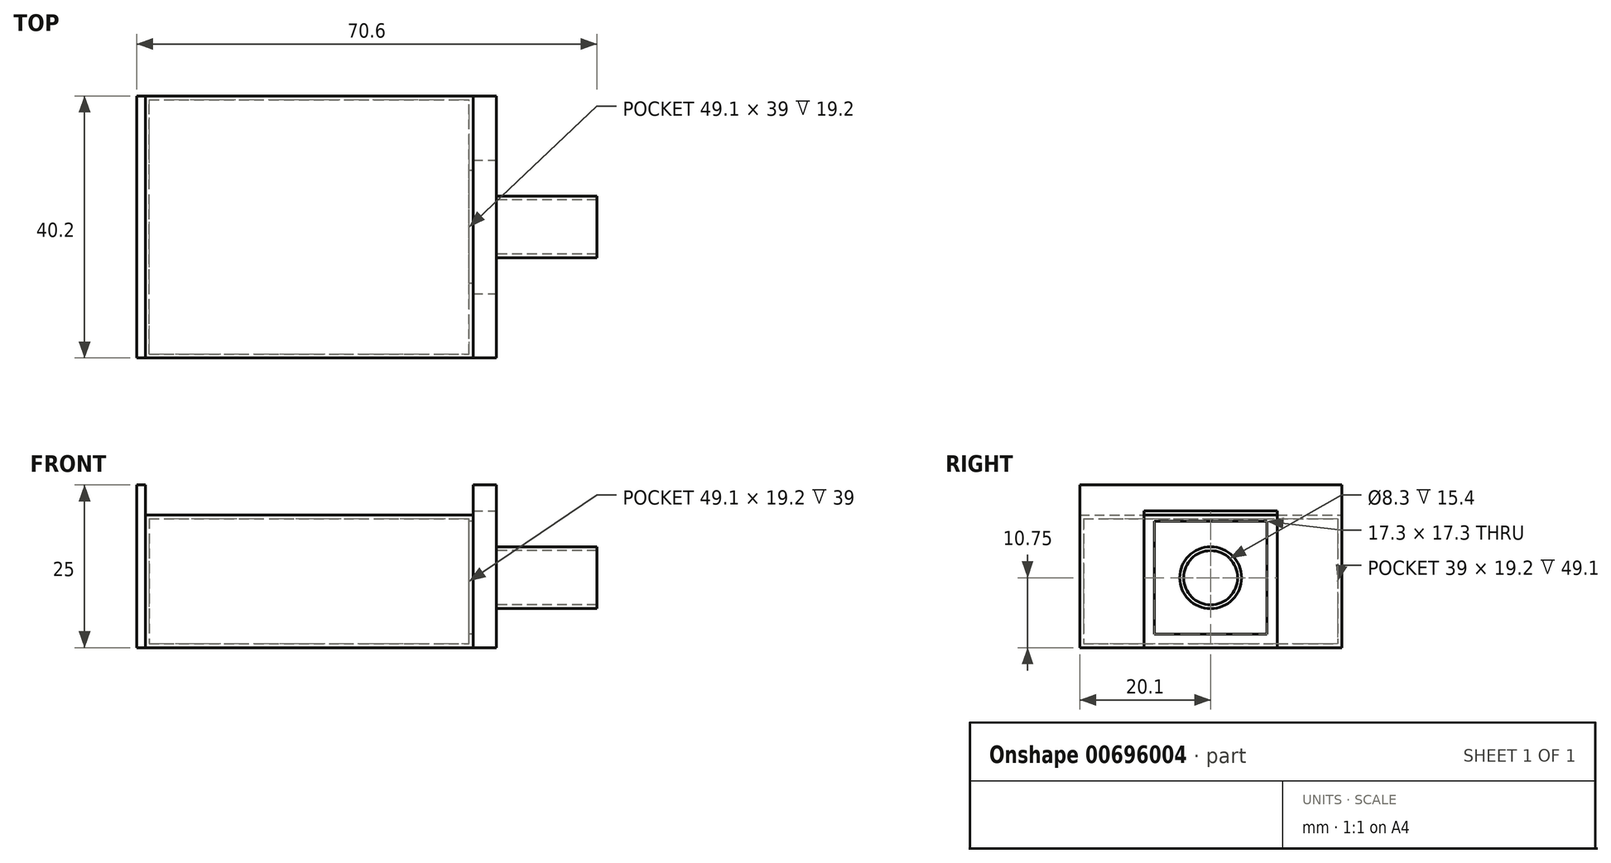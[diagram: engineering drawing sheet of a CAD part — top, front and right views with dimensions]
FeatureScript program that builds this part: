
annotation { "Feature Type Name" : "Feature", "Feature Type Description" : "" }
export const myFeature = defineFeature(function(context is Context, id is Id, definition is map)
    precondition{}
    {
        {
            var Q0;
            Q0=qCreatedBy(makeId("Front.planeOp"),FACE);
            var sketch = newSketch(context, id + "F0", { "sketchPlane" : qUnion([Q0])});
            skLineSegment(sketch, "E0", {"start": v(-22.7, 20.4) * mm, "end": v(27.6, 20.4) * mm});
            skLineSegment(sketch, "E1", {"start": v(-22.7, 20.4) * mm, "end": v(-22.7, 0) * mm});
            skLineSegment(sketch, "E2", {"start": v(-22.7, 0) * mm, "end": v(27.6, 0) * mm});
            skLineSegment(sketch, "E3", {"start": v(27.6, 0) * mm, "end": v(27.6, 20.4) * mm});
            skPoint(sketch, "E4", {"position": v(0, 0) * mm});
            skSolve(sketch);
        }
        {
            var Q0;
            Q0=makeQuery(id+"F0.imprint","IMPRINT",FACE,{"disambiguationData":[TD([[makeQuery(id+"F0.imprint","IMPRINT",EDGE,{"derivedFrom":sQuery(id+"F0.wireOp",EDGE,"E0")}),-1.0]])]});
            extrude(context, id + "F1", {"entities" : qUnion([Q0]), "depth" : 40.2 * mm, "offsetDistance" : 25 * mm, "symmetric" : true});
        }
        {
            var Q0;
            Q0=makeQuery(id+"F1.opExtrude","SWEPT_FACE",FACE,{"disambiguationData":[OSD([sQuery(id+"F0.wireOp",EDGE,"E3")])]});
            var sketch = newSketch(context, id + "F2", { "sketchPlane" : qUnion([Q0])});
            skLineSegment(sketch, "E5", {"start": v(-9.25, 1.5) * mm, "end": v(0, 1.5) * mm});
            skLineSegment(sketch, "E6", {"start": v(-9.25, 1.5) * mm, "end": v(-9.25, 20) * mm});
            skLineSegment(sketch, "E7", {"start": v(-9.25, 20) * mm, "end": v(0, 20) * mm});
            skLineSegment(sketch, "E8.MirrorCS", {"start": v(9.25, 20) * mm, "end": v(0, 20) * mm});
            skLineSegment(sketch, "E9.MirrorCS", {"start": v(9.25, 1.5) * mm, "end": v(9.25, 20) * mm});
            skLineSegment(sketch, "E10.MirrorCS", {"start": v(9.25, 1.5) * mm, "end": v(0, 1.5) * mm});
            skCircle(sketch, "E11", {"center": v(0, 10.75) * mm, "radius": 4.75 * mm});
            skPoint(sketch, "E12", {"position": v(-9.25, 10.75) * mm});
            skLineSegment(sketch, "E13", {"start": v(-9.25, 10.75) * mm, "end": v(9.25, 10.75) * mm, "construction": true});
            skSolve(sketch);
        }
        {
            var Q0;
            Q0=makeQuery(id+"F2.imprint","IMPRINT",FACE,{"disambiguationData":[TD([[makeQuery(id+"F2.imprint","IMPRINT",EDGE,{"derivedFrom":sQuery(id+"F2.wireOp",EDGE,"E5")}),1.0]])]});
            extrude(context, id + "F3", {"entities" : qUnion([Q0]), "operationType" : NewBodyOperationType.ADD, "depth" : 1.5 * mm, "offsetDistance" : 25 * mm});
        }
        {
            var Q0;
            Q0=makeQuery(id+"F3.boolean.opBoolean","SPLIT",FACE,{"disambiguationData":[TD([makeQuery(id+"F3.opExtrude","SWEPT_FACE",FACE,{"disambiguationData":[OSD([sQuery(id+"F2.wireOp",EDGE,"E11")])]})])],"derivedFrom":makeQuery(id+"F1.opExtrude","SWEPT_FACE",FACE,{"disambiguationData":[OSD([sQuery(id+"F0.wireOp",EDGE,"E3")])]})});
            extrude(context, id + "F4", {"entities" : qUnion([Q0]), "operationType" : NewBodyOperationType.ADD, "depth" : 19 * mm, "offsetDistance" : 25 * mm});
        }
        {
            var Q0;
            Q0=makeQuery(id+"F4.opExtrude","CAP_FACE",FACE,{"disambiguationData":[OSD([sQuery(id+"F0.wireOp",EDGE,"E3")])],"isStart":false});
            shell(context, id + "F5", {"entities" : qUnion([Q0]), "thickness" : .6 * mm});
        }
        {
            var Q0;
            Q0=qCreatedBy(makeId("Top.planeOp"),FACE);
            var sketch = newSketch(context, id + "F6", { "sketchPlane" : qUnion([Q0])});
            skLineSegment(sketch, "E14.bottom", {"start": v(27.6, -20.1) * mm, "end": v(31.2, -20.1) * mm});
            skLineSegment(sketch, "E14.top", {"start": v(27.6, 20.1) * mm, "end": v(31.2, 20.1) * mm});
            skLineSegment(sketch, "E14.left", {"start": v(27.6, -20.1) * mm, "end": v(27.6, 20.1) * mm});
            skLineSegment(sketch, "E14.right", {"start": v(31.2, -20.1) * mm, "end": v(31.2, 20.1) * mm});
            skLineSegment(sketch, "E15.bottom", {"start": v(-22.7, -20.1) * mm, "end": v(-24, -20.1) * mm});
            skLineSegment(sketch, "E15.top", {"start": v(-22.7, 20.1) * mm, "end": v(-24, 20.1) * mm});
            skLineSegment(sketch, "E15.left", {"start": v(-22.7, -20.1) * mm, "end": v(-22.7, 20.1) * mm});
            skLineSegment(sketch, "E15.right", {"start": v(-24, -20.1) * mm, "end": v(-24, 20.1) * mm});
            skSolve(sketch);
        }
        {
            var Q0;
            Q0=makeQuery(id+"F6.imprint","IMPRINT",FACE,{"disambiguationData":[TD([[makeQuery(id+"F6.imprint","IMPRINT",EDGE,{"derivedFrom":sQuery(id+"F6.wireOp",EDGE,"E14.bottom")}),1.0]])]});
            var Q1;
            Q1=makeQuery(id+"F6.imprint","IMPRINT",FACE,{"disambiguationData":[TD([[makeQuery(id+"F6.imprint","IMPRINT",EDGE,{"derivedFrom":sQuery(id+"F6.wireOp",EDGE,"E15.bottom")}),-1.0]])]});
            extrude(context, id + "F7", {"entities" : qUnion([Q0, Q1]), "depth" : 25 * mm, "offsetDistance" : 25 * mm});
        }
        {
            var Q0;
            Q0=makeQuery(id+"F7.opExtrude","SWEPT_FACE",FACE,{"disambiguationData":[OSD([sQuery(id+"F6.wireOp",EDGE,"E14.right")])]});
            var sketch = newSketch(context, id + "F8", { "sketchPlane" : qUnion([Q0])});
            skLineSegment(sketch, "E16.bottom", {"start": v(-9.25, 20) * mm, "end": v(9.25, 20) * mm});
            skLineSegment(sketch, "E16.top", {"start": v(-9.25, 0) * mm, "end": v(9.25, 0) * mm});
            skLineSegment(sketch, "E16.left", {"start": v(-9.25, 20) * mm, "end": v(-9.25, 0) * mm});
            skLineSegment(sketch, "E16.right", {"start": v(9.25, 20) * mm, "end": v(9.25, 0) * mm});
            skLineSegment(sketch, "E17.0", {"start": v(10.25, 21) * mm, "end": v(10.25, 0) * mm});
            skLineSegment(sketch, "E17.1", {"start": v(-10.25, 21) * mm, "end": v(10.25, 21) * mm});
            skLineSegment(sketch, "E17.2", {"start": v(-10.25, 21) * mm, "end": v(-10.25, 0) * mm});
            skLineSegment(sketch, "E18", {"start": v(0, 25) * mm, "end": v(0, 0) * mm, "construction": true});
            skLineSegment(sketch, "E19", {"start": v(0, 25) * mm, "end": v(20.1, 25) * mm, "construction": true});
            skLineSegment(sketch, "E20", {"start": v(10.05, 25) * mm, "end": v(10.05, 0) * mm, "construction": true});
            skCircle(sketch, "E21", {"center": v(10.05, 19) * mm, "radius": 3 * mm});
            skCircle(sketch, "E22", {"center": v(0, 19) * mm, "radius": 3 * mm});
            skLineSegment(sketch, "E23", {"start": v(0, 19) * mm, "end": v(20.1, 19) * mm, "construction": true});
            skCircle(sketch, "E24.MirrorC", {"center": v(-10.05, 19) * mm, "radius": 3 * mm});
            skSolve(sketch);
        }
        {
            var Q0;
            {var subQ1=makeQuery(id+"F7.opExtrude","CAP_EDGE",EDGE,{"disambiguationData":[OSD([sQuery(id+"F6.wireOp",EDGE,"E14.right")])],"isStart":true});var subQ5=sQuery(id+"F8.wireOp",EDGE,"E17.2");var subQ6=makeQuery(id+"F8.imprint","INTERSECT",VERTEX,{"derivedFrom":[subQ1,subQ5]});Q0=makeQuery(id+"F8.imprint","IMPRINT",FACE,{"disambiguationData":[TD([[makeQuery(id+"F8.imprint","IMPRINT",EDGE,{"disambiguationData":[TD([[subQ6,1.0]])],"derivedFrom":subQ5}),1.0]])]});}
            var Q1;
            {var subQ5=sQuery(id+"F8.wireOp",EDGE,"E16.left");var subQ6=sQuery(id+"F8.wireOp",EDGE,"E16.bottom");var subQ7=makeQuery(id+"F8.imprint","INTERSECT",VERTEX,{"derivedFrom":[subQ6,subQ5]});Q1=makeQuery(id+"F8.imprint","IMPRINT",FACE,{"disambiguationData":[TD([[makeQuery(id+"F8.imprint","IMPRINT",EDGE,{"disambiguationData":[TD([[subQ7,-1.0]])],"derivedFrom":subQ6}),1.0]])]});}
            var Q2;
            {var subQ0=sQuery(id+"F8.wireOp",EDGE,"E24.MirrorC");var subQ1=sQuery(id+"F8.wireOp",EDGE,"E16.bottom");var subQ2=makeQuery(id+"F8.imprint","INTERSECT",VERTEX,{"derivedFrom":[subQ1,subQ0]});Q2=makeQuery(id+"F8.imprint","IMPRINT",FACE,{"disambiguationData":[TD([[makeQuery(id+"F8.imprint","IMPRINT",EDGE,{"disambiguationData":[TD([[subQ2,-1.0]])],"derivedFrom":subQ1}),1.0]])]});}
            var Q3;
            {var subQ1=sQuery(id+"F8.wireOp",EDGE,"E16.top");Q3=makeQuery(id+"F8.imprint","IMPRINT",FACE,{"disambiguationData":[TD([[makeQuery(id+"F8.imprint","IMPRINT",EDGE,{"derivedFrom":subQ1}),1.0]])]});}
            var Q4;
            {var subQ0=sQuery(id+"F8.wireOp",EDGE,"E16.right");var subQ1=sQuery(id+"F8.wireOp",EDGE,"E16.bottom");var subQ2=makeQuery(id+"F8.imprint","INTERSECT",VERTEX,{"derivedFrom":[subQ1,subQ0]});Q4=makeQuery(id+"F8.imprint","IMPRINT",FACE,{"disambiguationData":[TD([[makeQuery(id+"F8.imprint","IMPRINT",EDGE,{"disambiguationData":[TD([[subQ2,1.0]])],"derivedFrom":subQ1}),-1.0]])]});}
            var Q5;
            {var subQ0=sQuery(id+"F8.wireOp",EDGE,"E22");var subQ1=sQuery(id+"F8.wireOp",EDGE,"E16.bottom");var subQ2=makeQuery(id+"F8.imprint","INTERSECT",VERTEX,{"disambiguationData":[OD(0.0)],"derivedFrom":[subQ1,subQ0]});Q5=makeQuery(id+"F8.imprint","IMPRINT",FACE,{"disambiguationData":[TD([[makeQuery(id+"F8.imprint","IMPRINT",EDGE,{"disambiguationData":[TD([[subQ2,-1.0]])],"derivedFrom":subQ1}),-1.0]])]});}
            var Q6;
            {var subQ0=sQuery(id+"F8.wireOp",EDGE,"E16.left");var subQ1=sQuery(id+"F8.wireOp",EDGE,"E16.bottom");var subQ2=makeQuery(id+"F8.imprint","INTERSECT",VERTEX,{"derivedFrom":[subQ1,subQ0]});Q6=makeQuery(id+"F8.imprint","IMPRINT",FACE,{"disambiguationData":[TD([[makeQuery(id+"F8.imprint","IMPRINT",EDGE,{"disambiguationData":[TD([[subQ2,-1.0]])],"derivedFrom":subQ1}),-1.0]])]});}
            var Q7;
            {var subQ1=makeQuery(id+"F7.opExtrude","CAP_EDGE",EDGE,{"disambiguationData":[OSD([sQuery(id+"F6.wireOp",EDGE,"E14.right")])],"isStart":true});var subQ5=sQuery(id+"F8.wireOp",EDGE,"E17.0");var subQ6=makeQuery(id+"F8.imprint","INTERSECT",VERTEX,{"derivedFrom":[subQ1,subQ5]});Q7=makeQuery(id+"F8.imprint","IMPRINT",FACE,{"disambiguationData":[TD([[makeQuery(id+"F8.imprint","IMPRINT",EDGE,{"disambiguationData":[TD([[subQ6,1.0]])],"derivedFrom":subQ5}),-1.0]])]});}
            var Q8;
            {var subQ6=sQuery(id+"F8.wireOp",EDGE,"E16.right");var subQ8=sQuery(id+"F8.wireOp",EDGE,"E16.bottom");var subQ9=makeQuery(id+"F8.imprint","INTERSECT",VERTEX,{"derivedFrom":[subQ8,subQ6]});Q8=makeQuery(id+"F8.imprint","IMPRINT",FACE,{"disambiguationData":[TD([[makeQuery(id+"F8.imprint","IMPRINT",EDGE,{"disambiguationData":[TD([[subQ9,1.0]])],"derivedFrom":subQ8}),1.0]])]});}
            var Q9;
            {var subQ0=sQuery(id+"F8.wireOp",EDGE,"E22");var subQ1=sQuery(id+"F8.wireOp",EDGE,"E16.bottom");var subQ2=makeQuery(id+"F8.imprint","INTERSECT",VERTEX,{"disambiguationData":[OD(1.0)],"derivedFrom":[subQ1,subQ0]});Q9=makeQuery(id+"F8.imprint","IMPRINT",FACE,{"disambiguationData":[TD([[makeQuery(id+"F8.imprint","IMPRINT",EDGE,{"disambiguationData":[TD([[subQ2,-1.0]])],"derivedFrom":subQ1}),1.0]])]});}
            var Q10;
            {var subQ0=sQuery(id+"F8.wireOp",EDGE,"E22");var subQ1=sQuery(id+"F8.wireOp",EDGE,"E16.bottom");var subQ2=makeQuery(id+"F8.imprint","INTERSECT",VERTEX,{"disambiguationData":[OD(0.0)],"derivedFrom":[subQ1,subQ0]});Q10=makeQuery(id+"F8.imprint","IMPRINT",FACE,{"disambiguationData":[TD([[makeQuery(id+"F8.imprint","IMPRINT",EDGE,{"disambiguationData":[TD([[subQ2,-1.0]])],"derivedFrom":subQ1}),1.0]])]});}
            var Q11;
            Q11=makeQuery(id+"F7.opExtrude","SWEPT_FACE",FACE,{"disambiguationData":[OSD([sQuery(id+"F6.wireOp",EDGE,"E14.left")])]});
            extrude(context, id + "F9", {"entities" : qUnion([Q0, Q1, Q2, Q3, Q4, Q5, Q6, Q7, Q8, Q9, Q10]), "operationType" : NewBodyOperationType.REMOVE, "endBound" : BoundingType.UP_TO_SURFACE, "oppositeDirection" : true, "depth" : 25 * mm, "endBoundEntityFace" : qUnion([Q11]), "offsetDistance" : 25 * mm});
        }
        {
            var Q0;
            Q0=makeQuery(id+"F8.imprint","IMPRINT",FACE,{"disambiguationData":[TD([[makeQuery(id+"F8.imprint","IMPRINT",EDGE,{"derivedFrom":sQuery(id+"F8.wireOp",EDGE,"E16.bottom")}),1.0]])]});
            var Q1;
            Q1=makeQuery(id+"F8.imprint","IMPRINT",FACE,{"disambiguationData":[TD([[makeQuery(id+"F8.imprint","IMPRINT",EDGE,{"derivedFrom":sQuery(id+"F8.wireOp",EDGE,"E16.bottom")}),-1.0]])]});
            var Q2;
            Q2=makeQuery(id+"F7.opExtrude","SWEPT_FACE",FACE,{"disambiguationData":[OSD([sQuery(id+"F6.wireOp",EDGE,"E14.left")])]});
            extrude(context, id + "F10", {"entities" : qUnion([Q0, Q1]), "operationType" : NewBodyOperationType.REMOVE, "endBound" : BoundingType.UP_TO_SURFACE, "oppositeDirection" : true, "depth" : 25 * mm, "endBoundEntityFace" : qUnion([Q2]), "offsetDistance" : 25 * mm});
        }
    });
